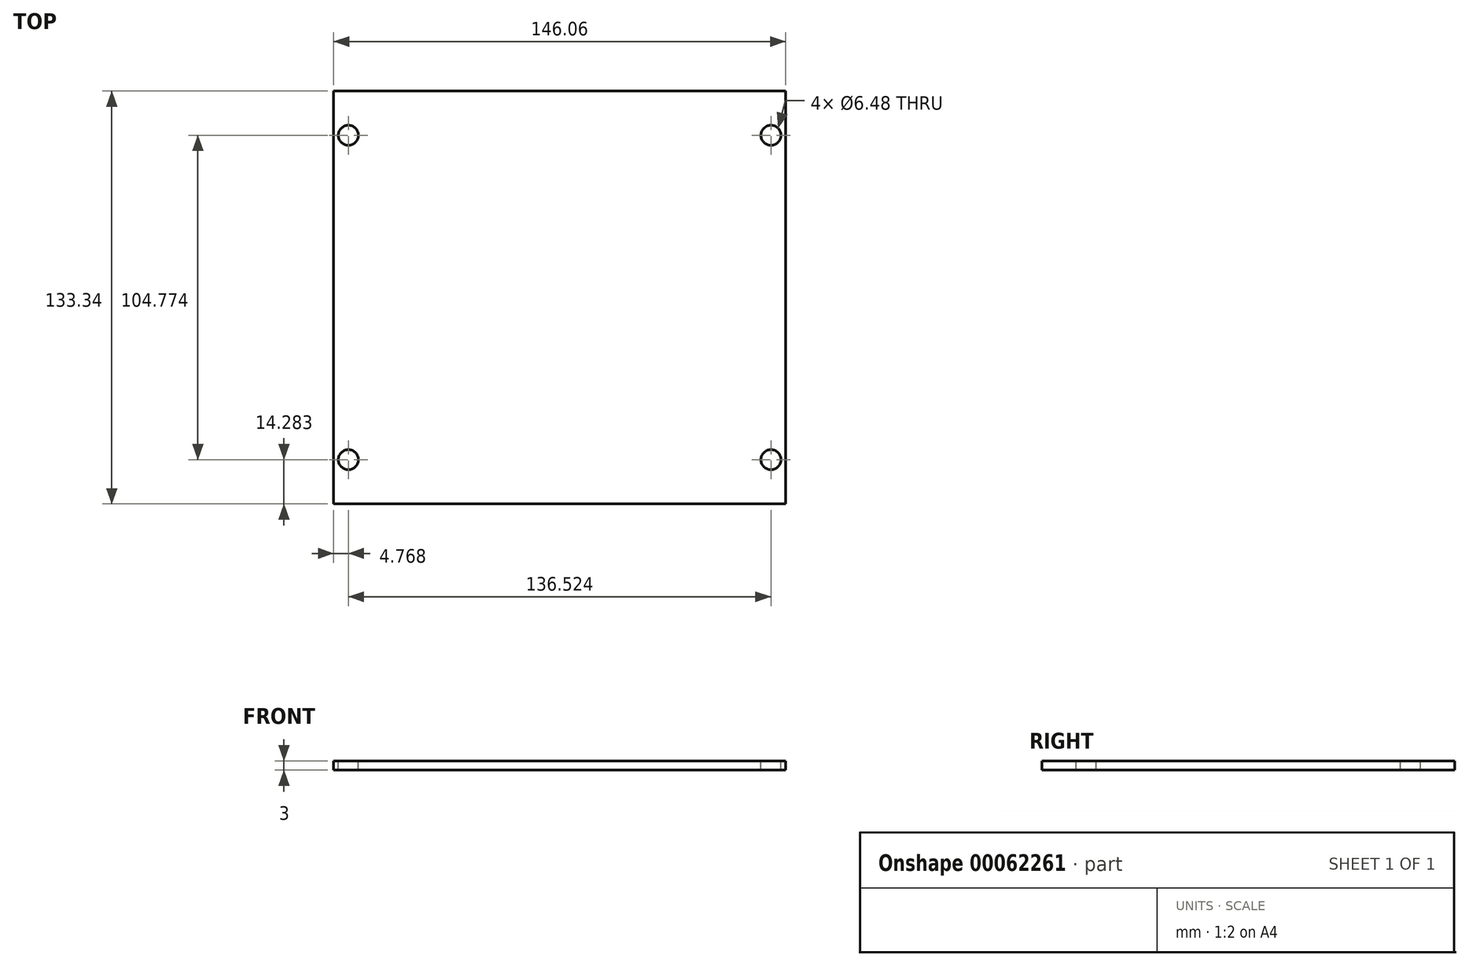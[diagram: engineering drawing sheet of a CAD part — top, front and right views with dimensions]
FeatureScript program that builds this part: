
annotation { "Feature Type Name" : "Feature", "Feature Type Description" : "" }
export const myFeature = defineFeature(function(context is Context, id is Id, definition is map)
    precondition{}
    {
        {
            var Q0;
            Q0=qCreatedBy(makeId("Top.planeOp"),FACE);
            var sketch = newSketch(context, id + "F0", { "sketchPlane" : qUnion([Q0])});
            skLineSegment(sketch, "E0", {"start": v(72.22, 1.59) * mm, "end": v(72.22, 46.04) * mm});
            skLineSegment(sketch, "E1", {"start": v(68.26, 1.59) * mm, "end": v(72.22, 1.59) * mm});
            skLineSegment(sketch, "E2", {"start": v(68.26, -11.11) * mm, "end": v(72.22, -11.11) * mm});
            skLineSegment(sketch, "E3", {"start": v(72.22, -46.04) * mm, "end": v(72.22, -11.11) * mm});
            skLineSegment(sketch, "E4", {"start": v(-68.26, -11.2) * mm, "end": v(-72.23, -11.2) * mm});
            skArc(sketch, "E5", {"start": v(-67.1, -10.98) * mm, "mid": v(-67.67, -11.15) * mm, "end": v(-68.26, -11.2) * mm});
            skLineSegment(sketch, "E6", {"start": v(-68.26, -46.04) * mm, "end": v(-72.23, -46.04) * mm});
            skLineSegment(sketch, "E7", {"start": v(-68.26, 46.04) * mm, "end": v(-72.23, 46.04) * mm});
            skLineSegment(sketch, "E8", {"start": v(-68.26, 58.74) * mm, "end": v(-72.23, 58.74) * mm});
            skLineSegment(sketch, "E9", {"start": v(-72.23, 58.74) * mm, "end": v(-72.23, 65.88) * mm});
            skLineSegment(sketch, "E10", {"start": v(-72.23, 65.88) * mm, "end": v(72.23, 65.88) * mm});
            skLineSegment(sketch, "E11", {"start": v(72.22, 58.74) * mm, "end": v(72.22, 65.88) * mm});
            skLineSegment(sketch, "E12", {"start": v(68.26, 58.74) * mm, "end": v(72.22, 58.74) * mm});
            skLineSegment(sketch, "E13", {"start": v(-68.26, -58.74) * mm, "end": v(-72.23, -58.74) * mm});
            skLineSegment(sketch, "E14", {"start": v(-72.23, -46.04) * mm, "end": v(-72.23, -11.2) * mm});
            skArc(sketch, "E15", {"start": v(68.26, -46.04) * mm, "mid": v(61.91, -52.39) * mm, "end": v(68.26, -58.74) * mm});
            skArc(sketch, "E16", {"start": v(68.26, 1.59) * mm, "mid": v(61.91, -4.76) * mm, "end": v(68.26, -11.11) * mm});
            skArc(sketch, "E17", {"start": v(68.26, 58.74) * mm, "mid": v(61.91, 52.39) * mm, "end": v(68.26, 46.04) * mm});
            skLineSegment(sketch, "E18", {"start": v(-72.23, 1.59) * mm, "end": v(-72.23, 46.04) * mm});
            skArc(sketch, "E19", {"start": v(-68.26, 46.04) * mm, "mid": v(-61.91, 52.39) * mm, "end": v(-68.26, 58.74) * mm});
            skLineSegment(sketch, "E20", {"start": v(-68.26, 1.59) * mm, "end": v(-72.23, 1.59) * mm});
            skLineSegment(sketch, "E21", {"start": v(68.26, -58.74) * mm, "end": v(72.22, -58.74) * mm});
            skLineSegment(sketch, "E22", {"start": v(72.22, -65.88) * mm, "end": v(-72.23, -65.88) * mm});
            skLineSegment(sketch, "E23", {"start": v(72.22, -65.88) * mm, "end": v(72.22, -58.74) * mm});
            skLineSegment(sketch, "E24", {"start": v(-72.23, -65.88) * mm, "end": v(-72.23, -58.74) * mm});
            skArc(sketch, "E25", {"start": v(-68.26, -58.74) * mm, "mid": v(-61.91, -52.39) * mm, "end": v(-68.26, -46.04) * mm});
            skLineSegment(sketch, "E26", {"start": v(68.26, -46.04) * mm, "end": v(72.22, -46.04) * mm});
            skLineSegment(sketch, "E27", {"start": v(68.26, 46.04) * mm, "end": v(72.22, 46.04) * mm});
            skCircle(sketch, "E28", {"center": v(68.26, 52.39) * mm, "radius": 3.24 * mm});
            skCircle(sketch, "E29", {"center": v(-68.26, -52.39) * mm, "radius": 3.24 * mm});
            skCircle(sketch, "E30", {"center": v(68.26, -52.39) * mm, "radius": 3.24 * mm});
            skCircle(sketch, "E31", {"center": v(68.26, -4.76) * mm, "radius": 3.24 * mm});
            skCircle(sketch, "E32", {"center": v(-68.26, -4.76) * mm, "radius": 3.22 * mm});
            skLineSegment(sketch, "E33", {"start": v(-73.03, 66.67) * mm, "end": v(73.03, 66.67) * mm});
            skLineSegment(sketch, "E34", {"start": v(73.03, -66.67) * mm, "end": v(73.03, 66.67) * mm});
            skLineSegment(sketch, "E35", {"start": v(73.03, -66.67) * mm, "end": v(-73.03, -66.67) * mm});
            skLineSegment(sketch, "E36", {"start": v(-73.03, -66.67) * mm, "end": v(-73.03, 66.67) * mm});
            skCircle(sketch, "E37", {"center": v(-68.26, 52.39) * mm, "radius": 3.24 * mm});
            skSolve(sketch);
        }
        {
            var Q0;
            Q0=qCreatedBy(makeId("Top.planeOp"),FACE);
            var sketch = newSketch(context, id + "F1", { "sketchPlane" : qUnion([Q0])});
            skLineSegment(sketch, "E38.bottom", {"start": v(-73.03, 66.68) * mm, "end": v(73.03, 66.68) * mm});
            skLineSegment(sketch, "E38.top", {"start": v(-73.03, -66.68) * mm, "end": v(73.03, -66.68) * mm});
            skLineSegment(sketch, "E38.left", {"start": v(-73.03, 66.68) * mm, "end": v(-73.03, -66.68) * mm});
            skLineSegment(sketch, "E38.right", {"start": v(73.03, 66.68) * mm, "end": v(73.03, -66.68) * mm});
            skPoint(sketch, "E38.middle", {"position": v(0, 0) * mm});
            skCircle(sketch, "E39", {"center": v(-68.26, 52.39) * mm, "radius": 3.24 * mm});
            skCircle(sketch, "E40.MirrorC", {"center": v(68.26, 52.39) * mm, "radius": 3.24 * mm});
            skCircle(sketch, "E41.MirrorC", {"center": v(-68.26, -52.39) * mm, "radius": 3.24 * mm});
            skCircle(sketch, "E42.MirrorC", {"center": v(68.26, -52.39) * mm, "radius": 3.24 * mm});
            skSolve(sketch);
        }
        {
            var Q0;
            Q0=makeQuery(id+"F1.imprint","IMPRINT",FACE,{"disambiguationData":[TD([[makeQuery(id+"F1.imprint","IMPRINT",EDGE,{"derivedFrom":sQuery(id+"F1.wireOp",EDGE,"E38.bottom")}),-1.0]])]});
            extrude(context, id + "F2", {"entities" : qUnion([Q0]), "oppositeDirection" : true, "depth" : 3 * mm, "offsetDistance" : 25 * mm});
        }
    });
